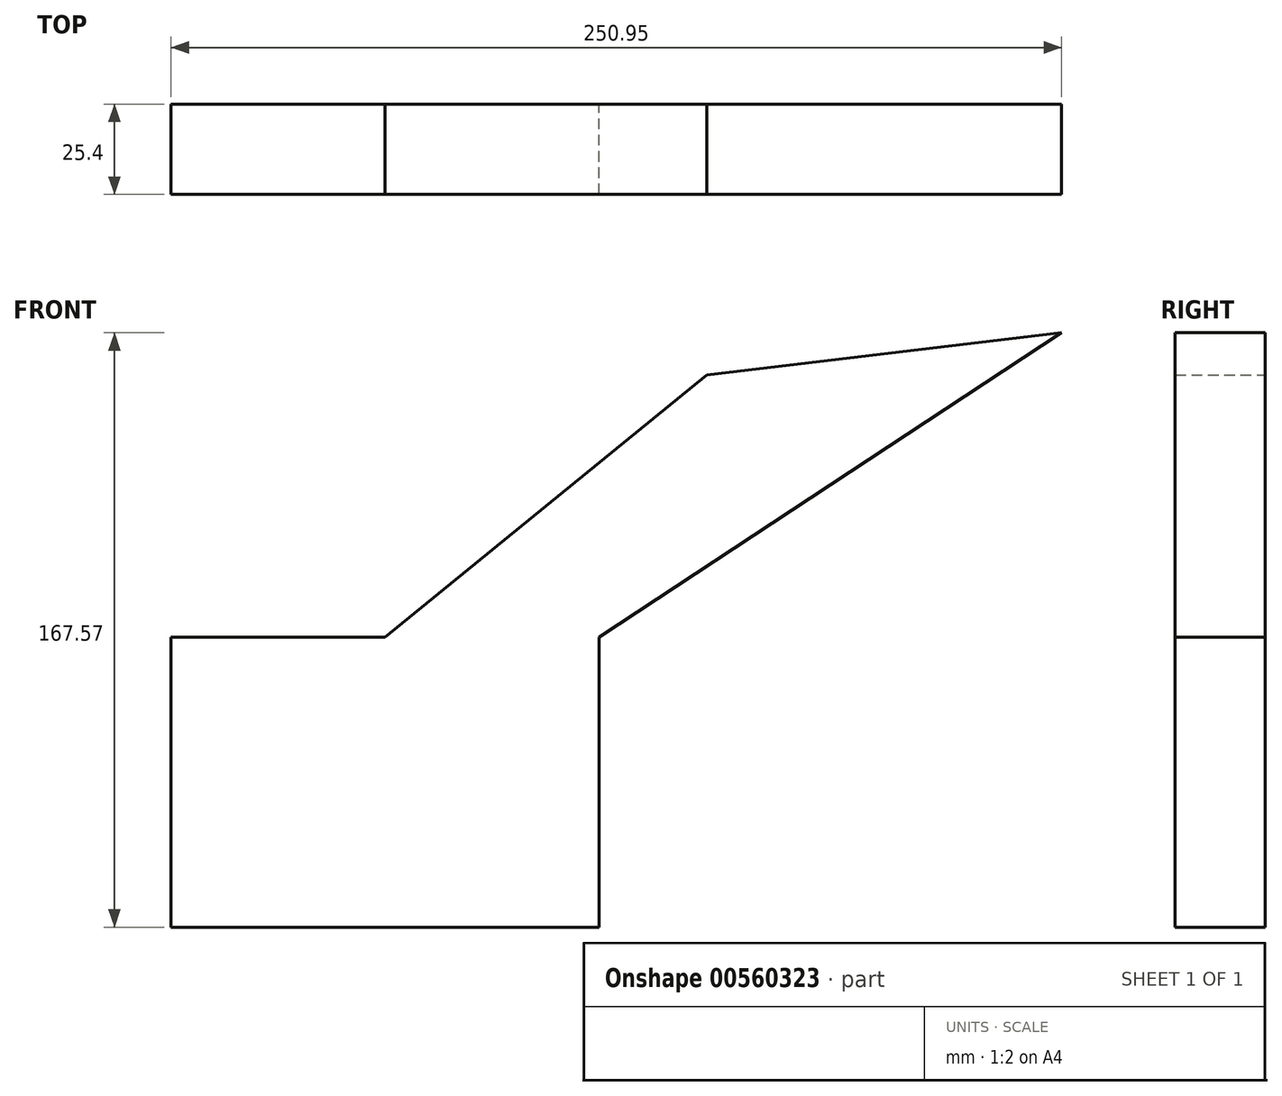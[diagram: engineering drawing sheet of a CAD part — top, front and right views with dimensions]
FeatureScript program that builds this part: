
annotation { "Feature Type Name" : "Feature", "Feature Type Description" : "" }
export const myFeature = defineFeature(function(context is Context, id is Id, definition is map)
    precondition{}
    {
        {
            var Q0;
            Q0=qCreatedBy(makeId("Front.planeOp"),FACE);
            var sketch = newSketch(context, id + "F0", { "sketchPlane" : qUnion([Q0])});
            skLineSegment(sketch, "E0.bottom", {"start": v(60.28, -40.87) * mm, "end": v(-60.28, -40.87) * mm});
            skLineSegment(sketch, "E0.top", {"start": v(60.28, 40.87) * mm, "end": v(-60.28, 40.87) * mm});
            skLineSegment(sketch, "E0.left", {"start": v(60.28, -40.87) * mm, "end": v(60.28, 40.87) * mm});
            skLineSegment(sketch, "E0.right", {"start": v(-60.28, -40.87) * mm, "end": v(-60.28, 40.87) * mm});
            skPoint(sketch, "E0.middle", {"position": v(0, 0) * mm});
            skLineSegment(sketch, "E1", {"start": v(0, 40.87) * mm, "end": v(90.64, 114.8) * mm});
            skLineSegment(sketch, "E2", {"start": v(90.64, 114.8) * mm, "end": v(190.67, 126.7) * mm});
            skLineSegment(sketch, "E3", {"start": v(190.67, 126.7) * mm, "end": v(60.28, 40.87) * mm});
            skSolve(sketch);
        }
        {
            var Q0;
            {var subQ2=sQuery(id+"F0.wireOp",EDGE,"E1");Q0=makeQuery(id+"F0.imprint","IMPRINT",FACE,{"disambiguationData":[TD([[makeQuery(id+"F0.imprint","IMPRINT",EDGE,{"derivedFrom":subQ2}),-1.0]])]});}
            var Q1;
            Q1=makeQuery(id+"F0.imprint","IMPRINT",FACE,{"disambiguationData":[TD([[makeQuery(id+"F0.imprint","IMPRINT",EDGE,{"derivedFrom":sQuery(id+"F0.wireOp",EDGE,"E0.bottom")}),-1.0]])]});
            extrude(context, id + "F1", {"entities" : qUnion([Q0, Q1]), "depth" : 25.4 * mm, "offsetDistance" : 25.4 * mm});
        }
    });
